# Revit family: Zara Ribbed 600mm WH Cabinet 1 Drawer
name_source: partatom
category: Plumbing Fixtures
units: mm (PartAtom-declared; Revit-internal decimal feet)

## family parameters
Always vertical = Yes
Cut with Voids When Loaded = No
Enable Cutting in Views = No
Maintain Annotation Orientation = No
OmniClass Number = 23.45.00.00
OmniClass Title = Sanitary, Laundry, and Cleaning Equipment
Part Type = Normal
Room Calculation Point = No
Round Connector Dimension = Use Diameter
Shared = No
Work Plane-Based = No

## types (4) — shared parameters
Category = Cabinets
Countertop = Sintered Stone
Manufacturer = Lecico SA
Notes = Dimensions are of Cabinet Only
Technical Dimensions = W600 x H400 x D460mm
URL = https://www.lecicosa.co.za
zero-valued in all types: Default Elevation

## per-type parameters (varying)
| type | Carcass | Colour | Door Base | Material | Product Code | Slats | Stone | URL (Stone) | URL (Vanity) | Vanity |
| Zara Ribbed 600mm WH White Cabinet 1 Drawer + 600 White Slab Top | White Melamine | White | White Melamine | MDF with Melamine Finish + Sintered Stone | CABZARAWH0600BC + SLA600WHITE00BC | White Melamine | Yes | https://www.lecicosa.co.za |  | No |
| Zara Ribbed 600mm WH Oak Cabinet 1 Drawer + 600 White Slap Top | Oak | Oak | Oak | MDF with Melamine Finish + Sintered Stone | CABZARAWHK600BC + SLA600WHITE00BC | Oak | Yes | https://www.lecicosa.co.za |  | No |
| Zara Ribbed 600mm WH White Cabinet 1 Drawer + Zara 60cm Vanity Basin | White Melamine | White | White Melamine | MDF with Melamine Finish + Vitreous China | CABZARAWH0600BC + ZARBASVAN1600UE | White Melamine | No |  | https://www.lecicosa.co.za | Yes |
| Zara Ribbed 600mm WH Oak Cabinet 1 Drawer + Zara 60cm Vanity Basin | Oak | Oak | Oak | MDF with Melamine Finish + Vitreous China | CABZARAWHK600BC + ZARBASVAN1600UE | Oak | No |  | https://www.lecicosa.co.za | Yes |

note: column(s) folded — value = type name in every type: Model

## geometry (parser evidence)
native form markers: Sweep x5
no freeform markers — native parametric forms only
